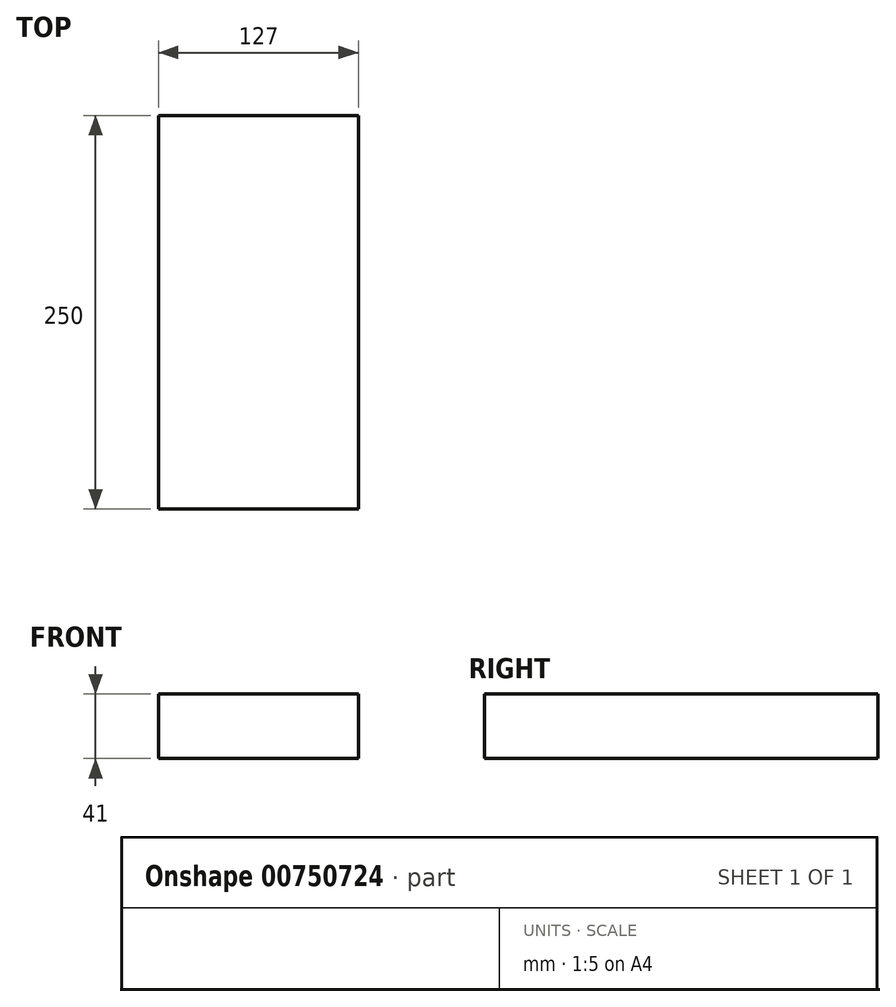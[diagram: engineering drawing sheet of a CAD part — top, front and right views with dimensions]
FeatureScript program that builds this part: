
annotation { "Feature Type Name" : "Feature", "Feature Type Description" : "" }
export const myFeature = defineFeature(function(context is Context, id is Id, definition is map)
    precondition{}
    {
        {
            var Q0;
            Q0=qCreatedBy(makeId("Top.planeOp"),FACE);
            var sketch = newSketch(context, id + "F0", { "sketchPlane" : qUnion([Q0])});
            skLineSegment(sketch, "E0.bottom", {"start": v(63.5, -125) * mm, "end": v(-63.5, -125) * mm});
            skLineSegment(sketch, "E0.top", {"start": v(63.5, 125) * mm, "end": v(-63.5, 125) * mm});
            skLineSegment(sketch, "E0.left", {"start": v(63.5, -125) * mm, "end": v(63.5, 125) * mm});
            skLineSegment(sketch, "E0.right", {"start": v(-63.5, -125) * mm, "end": v(-63.5, 125) * mm});
            skPoint(sketch, "E0.middle", {"position": v(0, 0) * mm});
            skSolve(sketch);
        }
        {
            var Q0;
            Q0 = qSketchRegion(id + "F0", true);
            extrude(context, id + "F1", {"entities" : qUnion([Q0]), "depth" : 41 * mm, "offsetDistance" : 25 * mm});
        }
    });
